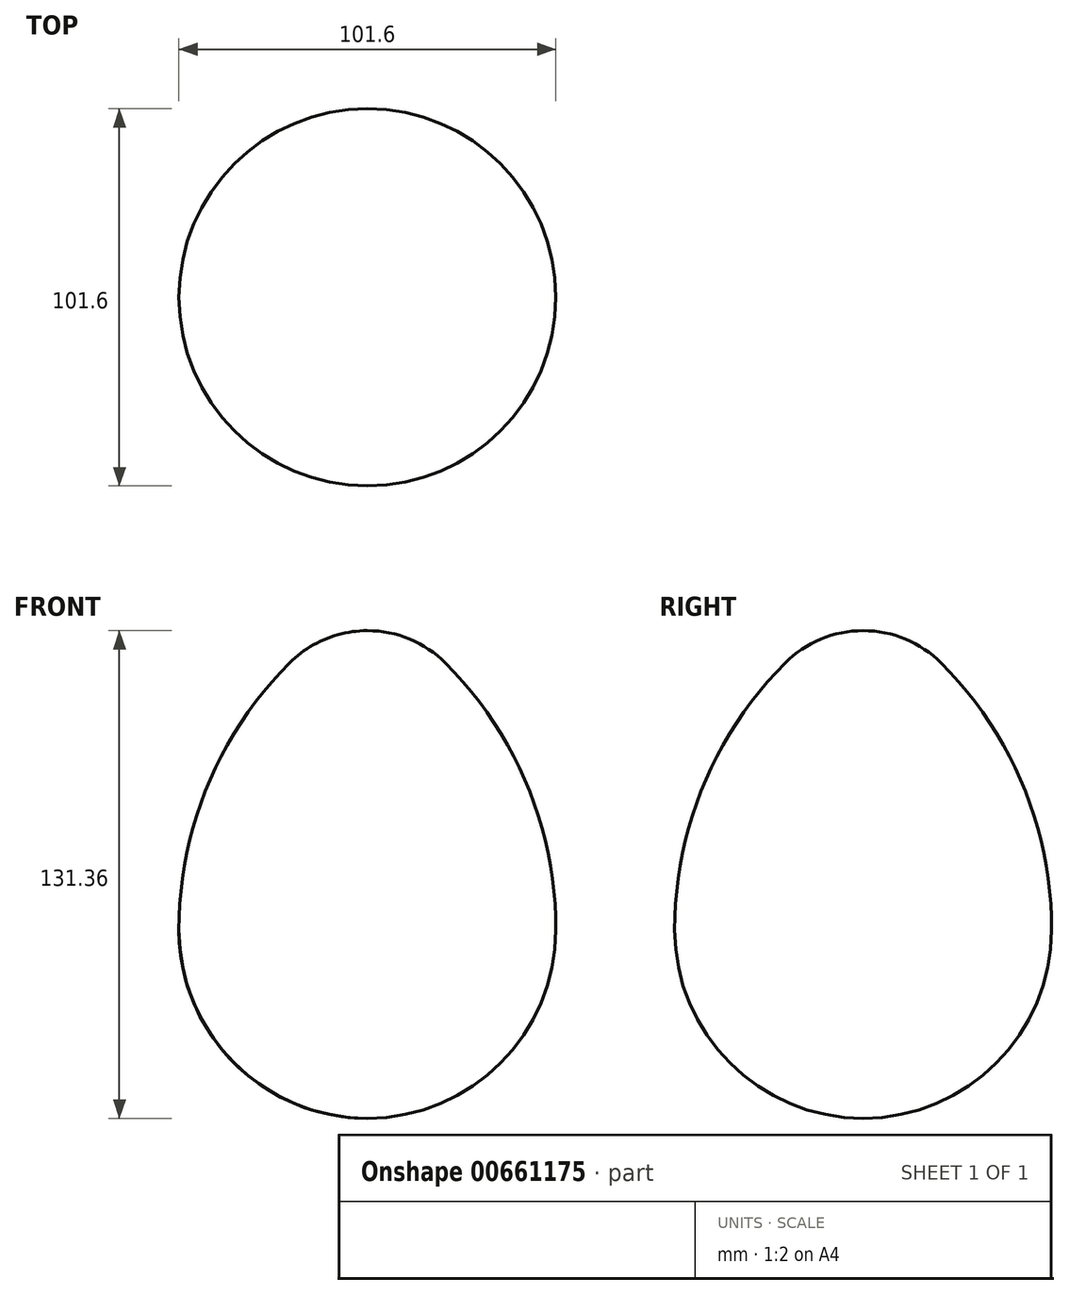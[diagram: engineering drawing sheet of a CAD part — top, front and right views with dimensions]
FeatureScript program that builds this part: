
annotation { "Feature Type Name" : "Feature", "Feature Type Description" : "" }
export const myFeature = defineFeature(function(context is Context, id is Id, definition is map)
    precondition{}
    {
        {
            var Q0;
            Q0=qCreatedBy(makeId("Front.planeOp"),FACE);
            var sketch = newSketch(context, id + "F0", { "sketchPlane" : qUnion([Q0])});
            skArc(sketch, "E0", {"start": v(-50.8, 0) * mm, "mid": v(0, -50.8) * mm, "end": v(50.8, 0) * mm});
            skArc(sketch, "E1", {"start": v(-21.04, 71.84) * mm, "mid": v(-43.07, 38.88) * mm, "end": v(-50.8, 0) * mm});
            skArc(sketch, "E2", {"start": v(50.8, 0) * mm, "mid": v(43.07, 38.88) * mm, "end": v(21.04, 71.84) * mm});
            skArc(sketch, "E3", {"start": v(21.04, 71.84) * mm, "mid": v(11.39, 78.3) * mm, "end": v(0, 80.56) * mm});
            skArc(sketch, "E4", {"start": v(0, 80.56) * mm, "mid": v(-11.39, 78.3) * mm, "end": v(-21.04, 71.84) * mm});
            skLineSegment(sketch, "E5", {"start": v(0, -50.8) * mm, "end": v(0, 80.56) * mm});
            skSolve(sketch);
        }
        {
            var Q0;
            {var subQ0=sQuery(id+"F0.wireOp",EDGE,"E1");Q0=makeQuery(id+"F0.imprint","IMPRINT",FACE,{"disambiguationData":[TD([[makeQuery(id+"F0.imprint","IMPRINT",EDGE,{"derivedFrom":subQ0}),1.0]])]});}
            var Q1;
            Q1=sQuery(id+"F0.wireOp",EDGE,"E5");
            revolve(context, id + "F1", {"entities" : qUnion([Q0]), "axis" : qUnion([Q1]), "revolveType" : RevolveType.FULL});
        }
    });
